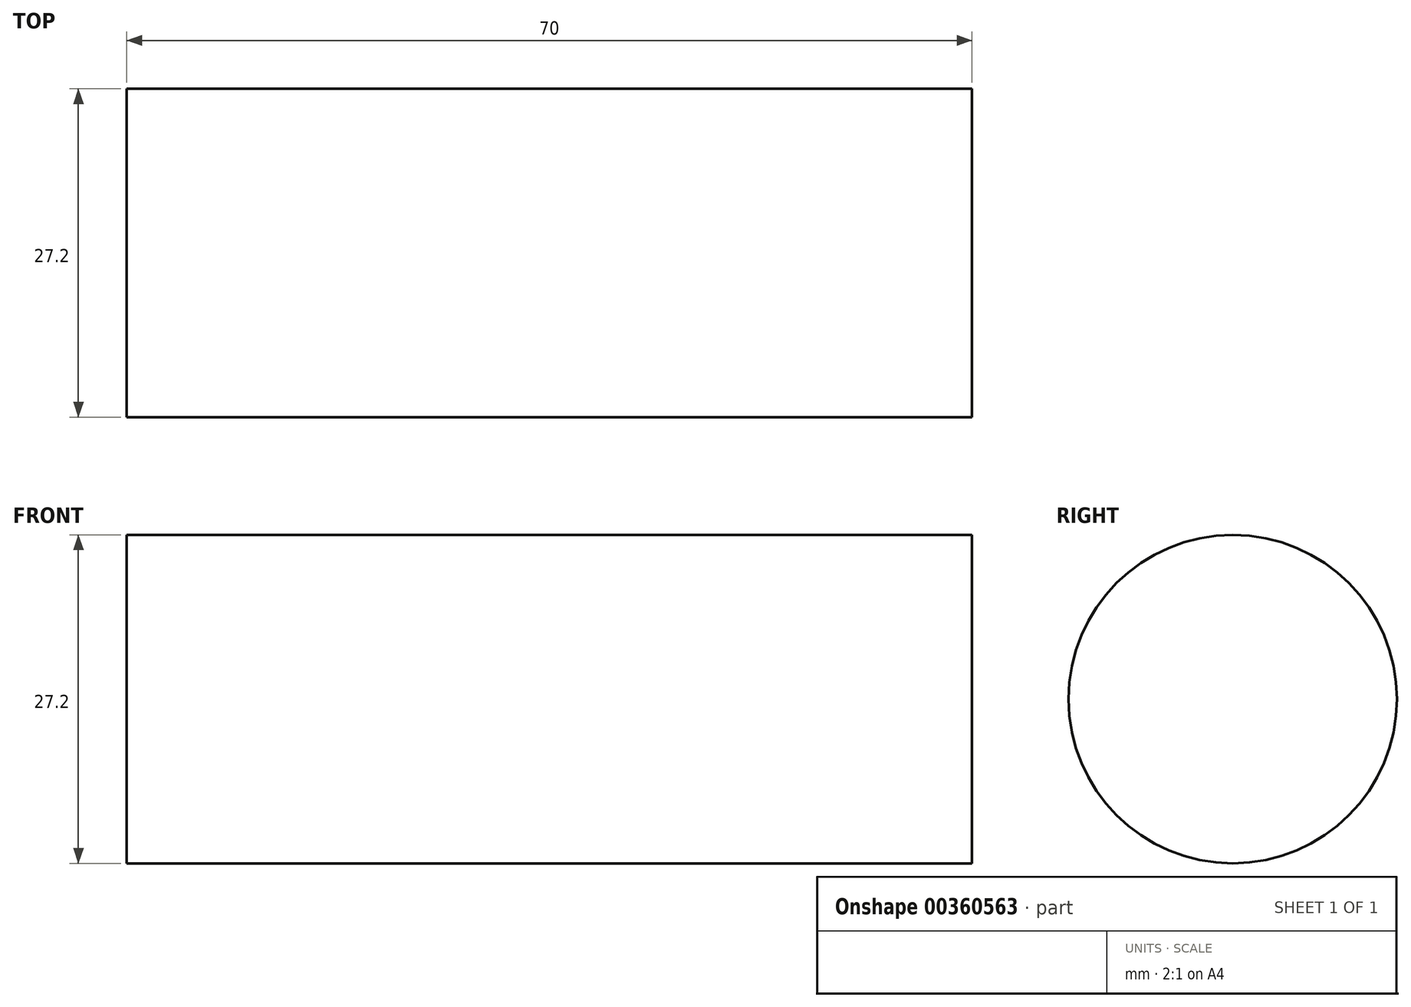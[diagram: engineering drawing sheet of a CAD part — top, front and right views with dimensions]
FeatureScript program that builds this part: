
annotation { "Feature Type Name" : "Feature", "Feature Type Description" : "" }
export const myFeature = defineFeature(function(context is Context, id is Id, definition is map)
    precondition{}
    {
        {
            var Q0;
            Q0=qCreatedBy(makeId("Right.planeOp"),FACE);
            var sketch = newSketch(context, id + "F0", { "sketchPlane" : qUnion([Q0])});
            skCircle(sketch, "E0", {"center": v(0, 0) * mm, "radius": 13.6 * mm});
            skSolve(sketch);
        }
        {
            var Q0;
            Q0 = qSketchRegion(id + "F0", true);
            extrude(context, id + "F1", {"entities" : qUnion([Q0]), "endBound" : BoundingType.SYMMETRIC, "depth" : 70 * mm, "offsetDistance" : 25 * mm});
        }
    });
